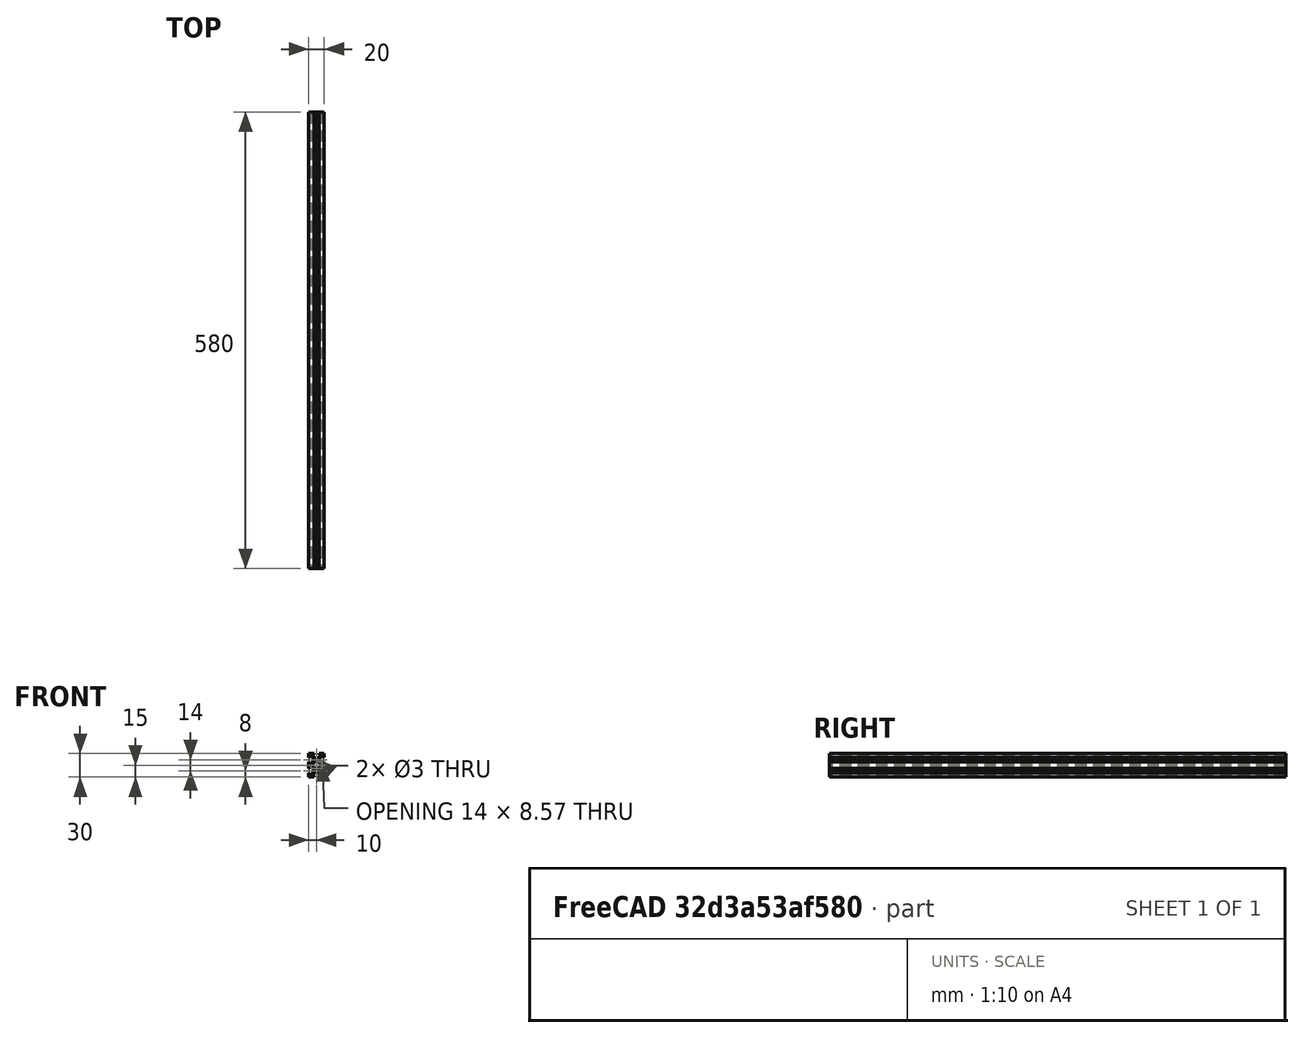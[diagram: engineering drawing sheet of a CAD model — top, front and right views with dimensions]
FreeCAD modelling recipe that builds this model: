
FCSTD DOCUMENT  (FreeCAD 1.1R40971 (Git))
Label: y-extrusion
License: All rights reserved
LicenseURL: http://en.wikipedia.org/wiki/All_rights_reserved
objects: Sketcher::SketchObject×1, PartDesign::Pad×1, PartDesign::Body×1, App::Point×1
note: 6 computed .brp shape members not serialized (recipe doc carries the construction recipe); baked Part::Feature solids carry a one-line shape summary decoded from their .brp

FEATURE [Sketcher::SketchObject] Sketch
  ArcFitTolerance = 0
  AttachmentSupport = -> [XZ_Plane]
  ExternalTypes = [0]
  FullyConstrained = false
  MakeInternals = false
  MapMode = 5
  Placement = pos=(0,0,0) rot=(1,0,0;1.5708rad)
  sketch-geometry (75):
    g0: LineSegment StartX=-10 StartY=30 StartZ=0 EndX=-3 EndY=30 EndZ=0
    g1: LineSegment StartX=10 StartY=30 StartZ=0 EndX=10 EndY=25 EndZ=0
    g2: LineSegment StartX=10 StartY=0 StartZ=0 EndX=3 EndY=0 EndZ=0
    g3: LineSegment StartX=-10 StartY=0 StartZ=0 EndX=-10 EndY=5 EndZ=0
    g4: LineSegment StartX=-3 StartY=0 StartZ=0 EndX=-3 EndY=1.5 EndZ=0
    g5: LineSegment StartX=-3 StartY=1.5 StartZ=0 EndX=-4.5 EndY=1.5 EndZ=0
    g6: LineSegment StartX=-4.5 StartY=1.5 StartZ=0 EndX=-4.5 EndY=3 EndZ=0
    g7: LineSegment StartX=-4.5 StartY=3 StartZ=0 EndX=-1.5 EndY=6 EndZ=0
    g8: LineSegment StartX=-1.5 StartY=6 StartZ=0 EndX=1.5 EndY=6 EndZ=0
    g9: LineSegment StartX=1.5 StartY=6 StartZ=0 EndX=4.5 EndY=3 EndZ=0
    g10: LineSegment StartX=4.5 StartY=3 StartZ=0 EndX=4.5 EndY=1.5 EndZ=0
    g11: LineSegment StartX=4.5 StartY=1.5 StartZ=0 EndX=3 EndY=1.5 EndZ=0
    g12: LineSegment StartX=3 StartY=1.5 StartZ=0 EndX=3 EndY=0 EndZ=0
    g13: LineSegment StartX=-3 StartY=0 StartZ=0 EndX=-10 EndY=0 EndZ=0
    g14: LineSegment StartX=-10 StartY=5 StartZ=0 EndX=-8.5 EndY=5 EndZ=0
    g15: LineSegment StartX=-8.5 StartY=5 StartZ=0 EndX=-8.5 EndY=3.5 EndZ=0
    g16: LineSegment StartX=-8.5 StartY=3.5 StartZ=0 EndX=-7 EndY=3.5 EndZ=0
    g17: LineSegment StartX=-7 StartY=3.5 StartZ=0 EndX=-4 EndY=6.5 EndZ=0
    g18: LineSegment StartX=-4 StartY=6.5 StartZ=0 EndX=-4 EndY=9.5 EndZ=0
    g19: LineSegment StartX=-4 StartY=9.5 StartZ=0 EndX=-7 EndY=12.5 EndZ=0
    g20: LineSegment StartX=-7 StartY=12.5 StartZ=0 EndX=-8.5 EndY=12.5 EndZ=0
    g21: LineSegment StartX=-8.5 StartY=12.5 StartZ=0 EndX=-8.5 EndY=11 EndZ=0
    g22: LineSegment StartX=-8.5 StartY=11 StartZ=0 EndX=-10 EndY=11 EndZ=0
    g23: LineSegment [constr] StartX=-9.99569 StartY=8 StartZ=0 EndX=10 EndY=8 EndZ=0
    g24: LineSegment StartX=-10 StartY=11 StartZ=0 EndX=-10 EndY=19 EndZ=0
    g25: LineSegment StartX=-10 StartY=25 StartZ=0 EndX=-8.5 EndY=25 EndZ=0
    g26: LineSegment StartX=-8.5 StartY=25 StartZ=0 EndX=-8.5 EndY=26.5 EndZ=0
    g27: LineSegment StartX=-8.5 StartY=26.5 StartZ=0 EndX=-7 EndY=26.5 EndZ=0
    g28: LineSegment StartX=-7 StartY=26.5 StartZ=0 EndX=-4 EndY=23.5 EndZ=0
    g29: LineSegment StartX=-4 StartY=23.5 StartZ=0 EndX=-4 EndY=20.5 EndZ=0
    g30: LineSegment StartX=-4 StartY=20.5 StartZ=0 EndX=-7 EndY=17.5 EndZ=0
    g31: LineSegment StartX=-7 StartY=17.5 StartZ=0 EndX=-8.5 EndY=17.5 EndZ=0
    g32: LineSegment StartX=-8.5 StartY=17.5 StartZ=0 EndX=-8.5 EndY=19 EndZ=0
    g33: LineSegment StartX=-8.5 StartY=19 StartZ=0 EndX=-10 EndY=19 EndZ=0
    g34: LineSegment [constr] StartX=-10 StartY=22 StartZ=0 EndX=9.99999 EndY=22 EndZ=0
    g35: LineSegment StartX=-10 StartY=25 StartZ=0 EndX=-10 EndY=30 EndZ=0
    g36: LineSegment StartX=-3 StartY=30 StartZ=0 EndX=-3 EndY=28.5 EndZ=0
    g37: LineSegment StartX=-3 StartY=28.5 StartZ=0 EndX=-4.5 EndY=28.5 EndZ=0
    g38: LineSegment StartX=-4.5 StartY=28.5 StartZ=0 EndX=-4.5 EndY=27 EndZ=0
    g39: LineSegment StartX=-4.5 StartY=27 StartZ=0 EndX=-1.5 EndY=24 EndZ=0
    g40: LineSegment StartX=-1.5 StartY=24 StartZ=0 EndX=1.5 EndY=24 EndZ=0
    g41: LineSegment StartX=1.5 StartY=24 StartZ=0 EndX=4.5 EndY=27 EndZ=0
    g42: LineSegment StartX=4.5 StartY=27 StartZ=0 EndX=4.5 EndY=28.5 EndZ=0
    g43: LineSegment StartX=4.5 StartY=28.5 StartZ=0 EndX=3 EndY=28.5 EndZ=0
    g44: LineSegment StartX=3 StartY=28.5 StartZ=0 EndX=3 EndY=30 EndZ=0
    g45: LineSegment StartX=3 StartY=30 StartZ=0 EndX=10 EndY=30 EndZ=0
    g46: LineSegment StartX=10 StartY=25 StartZ=0 EndX=8.5 EndY=25 EndZ=0
    g47: LineSegment StartX=8.5 StartY=25 StartZ=0 EndX=8.5 EndY=26.5 EndZ=0
    g48: LineSegment StartX=8.5 StartY=26.5 StartZ=0 EndX=7 EndY=26.5 EndZ=0
    g49: LineSegment StartX=7 StartY=26.5 StartZ=0 EndX=4 EndY=23.5 EndZ=0
    g50: LineSegment StartX=4 StartY=23.5 StartZ=0 EndX=4 EndY=20.5 EndZ=0
    g51: LineSegment StartX=4 StartY=20.5 StartZ=0 EndX=7 EndY=17.5 EndZ=0
    g52: LineSegment StartX=7 StartY=17.5 StartZ=0 EndX=8.5 EndY=17.5 EndZ=0
    g53: LineSegment StartX=8.5 StartY=17.5 StartZ=0 EndX=8.5 EndY=19 EndZ=0
    g54: LineSegment StartX=8.5 StartY=19 StartZ=0 EndX=10 EndY=19 EndZ=0
    g55: LineSegment StartX=10 StartY=19 StartZ=0 EndX=10 EndY=11 EndZ=0
    g56: LineSegment StartX=10 StartY=11 StartZ=0 EndX=8.5 EndY=11 EndZ=0
    g57: LineSegment StartX=8.5 StartY=11 StartZ=0 EndX=8.5 EndY=12.5 EndZ=0
    g58: LineSegment StartX=8.5 StartY=12.5 StartZ=0 EndX=7 EndY=12.5 EndZ=0
    g59: LineSegment StartX=7 StartY=12.5 StartZ=0 EndX=4 EndY=9.5 EndZ=0
    g60: LineSegment StartX=4 StartY=9.5 StartZ=0 EndX=4 EndY=6.5 EndZ=0
    g61: LineSegment StartX=4 StartY=6.5 StartZ=0 EndX=7 EndY=3.5 EndZ=0
    g62: LineSegment StartX=7 StartY=3.5 StartZ=0 EndX=8.5 EndY=3.5 EndZ=0
    g63: LineSegment StartX=8.5 StartY=3.5 StartZ=0 EndX=8.5 EndY=5 EndZ=0
    g64: LineSegment StartX=8.5 StartY=5 StartZ=0 EndX=10 EndY=5 EndZ=0
    g65: LineSegment StartX=10 StartY=5 StartZ=0 EndX=10 EndY=0 EndZ=0
    g66: Circle CenterX=0 CenterY=8 CenterZ=0 NormalX=0 NormalY=0 NormalZ=1 AngleXU=0 Radius=1.5
    g67: Circle CenterX=0 CenterY=22 CenterZ=0 NormalX=0 NormalY=0 NormalZ=1 AngleXU=0 Radius=1.5
    g68: LineSegment StartX=-7 StartY=15 StartZ=0 EndX=-2.71635 EndY=19.2836 EndZ=0
    g69: LineSegment StartX=-2.71635 StartY=19.2836 StartZ=0 EndX=2.71635 EndY=19.2836 EndZ=0
    g70: LineSegment StartX=2.71635 StartY=19.2836 StartZ=0 EndX=7 EndY=15 EndZ=0
    g71: LineSegment StartX=7 StartY=15 StartZ=0 EndX=2.71635 EndY=10.7164 EndZ=0
    g72: LineSegment StartX=2.71635 StartY=10.7164 StartZ=0 EndX=-2.71635 EndY=10.7164 EndZ=0
    g73: LineSegment StartX=-2.71635 StartY=10.7164 StartZ=0 EndX=-7 EndY=15 EndZ=0
    g74: LineSegment [constr] StartX=-10 StartY=15 StartZ=0 EndX=10 EndY=15 EndZ=0
  constraints (212):
    c: Coincident(g45,g1)
    c: Coincident(g65,g2)
    c: Coincident(g13,g3)
    c: Coincident(g35,g0)
    c: Horizontal(g0)
    c: Horizontal(g2)
    c: Vertical(g1)
    c: Vertical(g3)
    c: Symmetric(g65,g13,g-1)
    c: DistanceX(g13,g2) = 20
    c: DistanceY(g3,g35) = 30
    c: Vertical(g4)
    c: Coincident(g4,g5)
    c: Horizontal(g5)
    c: Coincident(g5,g6)
    c: Vertical(g6)
    c: Coincident(g6,g7)
    c: Coincident(g7,g8)
    c: Coincident(g8,g9)
    c: Coincident(g9,g10)
    c: Vertical(g10)
    c: Coincident(g10,g11)
    c: Horizontal(g11)
    c: Coincident(g11,g12)
    c: Vertical(g12)
    c: Equal(g6,g5)
    c: Equal(g5,g4)
    c: Equal(g4,g12)
    c: Equal(g12,g11)
    c: Equal(g11,g10)
    c: Distance(g4) = 1.5
    c: DistanceX(g4,g12) = 6
    c: Symmetric(g12,g4,g-2)
    c: Perpendicular(g9,g7)
    c: Symmetric(g7,g8,g-2)
    c: DistanceY(g4,g7) = 6
    c: Coincident(g13,g4)
    c: PointOnObject(g4,g-1)
    c: Coincident(g12,g2)
    c: Coincident(g14,g15)
    c: Coincident(g15,g16)
    c: Horizontal(g16)
    c: Coincident(g16,g17)
    c: Coincident(g17,g18)
    c: Vertical(g18)
    c: Coincident(g18,g19)
    c: Coincident(g19,g20)
    c: Coincident(g20,g21)
    c: Vertical(g21)
    c: Coincident(g21,g22)
    c: Horizontal(g22)
    c: Horizontal(g20)
    c: Vertical(g15)
    c: Equal(g6,g16)
    c: Equal(g16,g15)
    c: Equal(g15,g14)
    c: Equal(g14,g22)
    c: Equal(g22,g21)
    c: Equal(g21,g20)
    c: Perpendicular(g17,g19)
    c: PointOnObject(g23,g1)
    c: Symmetric(g22,g14,g23)
    c: Horizontal(g14)
    c: Symmetric(g17,g18,g23)
    c: Equal(g19,g7)
    c: Equal(g8,g18)
    c: Coincident(g3,g14)
    c: DistanceY(g3,g3) = 5
    c: Horizontal(g25)
    c: Coincident(g25,g26)
    c: Vertical(g26)
    c: Coincident(g26,g27)
    c: Coincident(g27,g28)
    c: Coincident(g28,g29)
    c: Vertical(g29)
    c: Coincident(g29,g30)
    c: Coincident(g30,g31)
    c: Horizontal(g31)
    c: Coincident(g31,g32)
    c: Coincident(g32,g33)
    c: Horizontal(g33)
    c: Symmetric(g29,g28,g34)
    c: Symmetric(g25,g33,g34)
    c: Vertical(g32)
    c: Horizontal(g27)
    c: Equal(g6,g31)
    c: Equal(g31,g32)
    c: Equal(g32,g33)
    c: Equal(g33,g25)
    c: Equal(g25,g26)
    c: Equal(g26,g27)
    c: Equal(g8,g29)
    c: Equal(g30,g7)
    c: Coincident(g35,g25)
    c: Coincident(g24,g33)
    c: Equal(g35,g3)
    c: Vertical(g24)
    c: Vertical(g35)
    c: Coincident(g22,g24)
    c: Perpendicular(g30,g28)
    c: Vertical(g36)
    c: Coincident(g36,g37)
    c: Horizontal(g37)
    c: Coincident(g37,g38)
    c: Vertical(g38)
    c: Coincident(g38,g39)
    c: Coincident(g39,g40)
    c: Horizontal(g40)
    c: Coincident(g40,g41)
    c: Coincident(g41,g42)
    c: Vertical(g42)
    c: Coincident(g42,g43)
    c: Horizontal(g43)
    c: Coincident(g43,g44)
    c: Vertical(g44)
    c: Coincident(g0,g36)
    c: Coincident(g45,g44)
    c: Symmetric(g0,g44,g-2)
    c: Equal(g38,g37)
    c: Equal(g37,g36)
    c: Equal(g36,g44)
    c: Equal(g44,g43)
    c: Equal(g43,g42)
    c: Equal(g0,g45)
    c: Equal(g39,g41)
    c: Equal(g41,g7)
    c: Perpendicular(g41,g39)
    c: Equal(g38,g6)
    c: Equal(g40,g8)
    c: Horizontal(g46)
    c: Coincident(g46,g47)
    c: Vertical(g47)
    c: Coincident(g47,g48)
    c: Horizontal(g48)
    c: Coincident(g48,g49)
    c: Coincident(g49,g50)
    c: Coincident(g50,g51)
    c: Coincident(g51,g52)
    c: Horizontal(g52)
    c: Coincident(g52,g53)
    c: Vertical(g53)
    c: Coincident(g53,g54)
    c: PointOnObject(g54,g1)
    c: Horizontal(g54)
    c: Symmetric(g49,g50,g34)
    c: Perpendicular(g51,g49)
    c: Equal(g48,g47)
    c: Equal(g47,g46)
    c: Equal(g46,g54)
    c: Equal(g54,g53)
    c: Equal(g53,g52)
    c: Equal(g52,g6)
    c: Equal(g49,g51)
    c: Equal(g8,g50)
    c: Coincident(g1,g46)
    c: PointOnObject(g55,g54)
    c: Equal(g51,g7)
    c: Equal(g1,g35)
    c: Horizontal(g56)
    c: Coincident(g56,g57)
    c: Vertical(g57)
    c: Coincident(g57,g58)
    c: Horizontal(g58)
    c: Coincident(g58,g59)
    c: Coincident(g59,g60)
    c: Coincident(g60,g61)
    c: Coincident(g61,g62)
    c: Horizontal(g62)
    c: Coincident(g62,g63)
    c: Vertical(g63)
    c: Coincident(g63,g64)
    c: Horizontal(g64)
    c: Coincident(g65,g64)
    c: Coincident(g55,g56)
    c: Symmetric(g55,g64,g23)
    c: Symmetric(g59,g60,g23)
    c: Equal(g58,g57)
    c: Equal(g57,g56)
    c: Equal(g56,g64)
    c: Equal(g64,g63)
    c: Equal(g63,g62)
    c: Equal(g62,g6)
    c: Equal(g8,g60)
    c: Vertical(g55)
    c: Vertical(g65)
    c: Equal(g65,g1)
    c: Equal(g61,g7)
    c: PointOnObject(g67,g-2)
    c: PointOnObject(g34,g3)
    c: Diameter(g66) = 3
    c: Coincident(g68,g69)
    c: Horizontal(g69)
    c: Coincident(g69,g70)
    c: Coincident(g70,g71)
    c: Coincident(g71,g72)
    c: Coincident(g72,g73)
    c: Coincident(g73,g68)
    c: Perpendicular(g73,g68)
    c: Perpendicular(g71,g70)
    c: Parallel(g59,g71)
    c: Parallel(g73,g19)
    c: Symmetric(g71,g72,g-2)
    c: Equal(g71,g73)
    c: PointOnObject(g74,g24)
    c: PointOnObject(g74,g55)
    c: Symmetric(g0,g3,g74)
    c: PointOnObject(g70,g74)
    c: Equal(g66,g67)
    c: Symmetric(g67,g66,g74)
    c: Equal(g72,g69)
    c: Vertical(g30,g68)
    c: DistanceY(g66,g67) = 14
FEATURE [PartDesign::Pad] Pad
  Direction = (0,-1,2e-16)
  Length = 580
  Length2 = 10
  Midplane = true
  Placement = pos=(0,0,0) rot=(1,0,0;1.5708rad)
  Profile = -> Sketch
  ReferenceAxis = -> Sketch [N_Axis]
  Suppressed = false
  Type = 0
FEATURE [PartDesign::Body] Body
  AllowCompound = false
  Group = -> [Sketch,Pad]
  Origin = -> Origin
  Tip = -> Pad
FEATURE [App::Point] Origin001  label="Origin"
  Role = Origin
